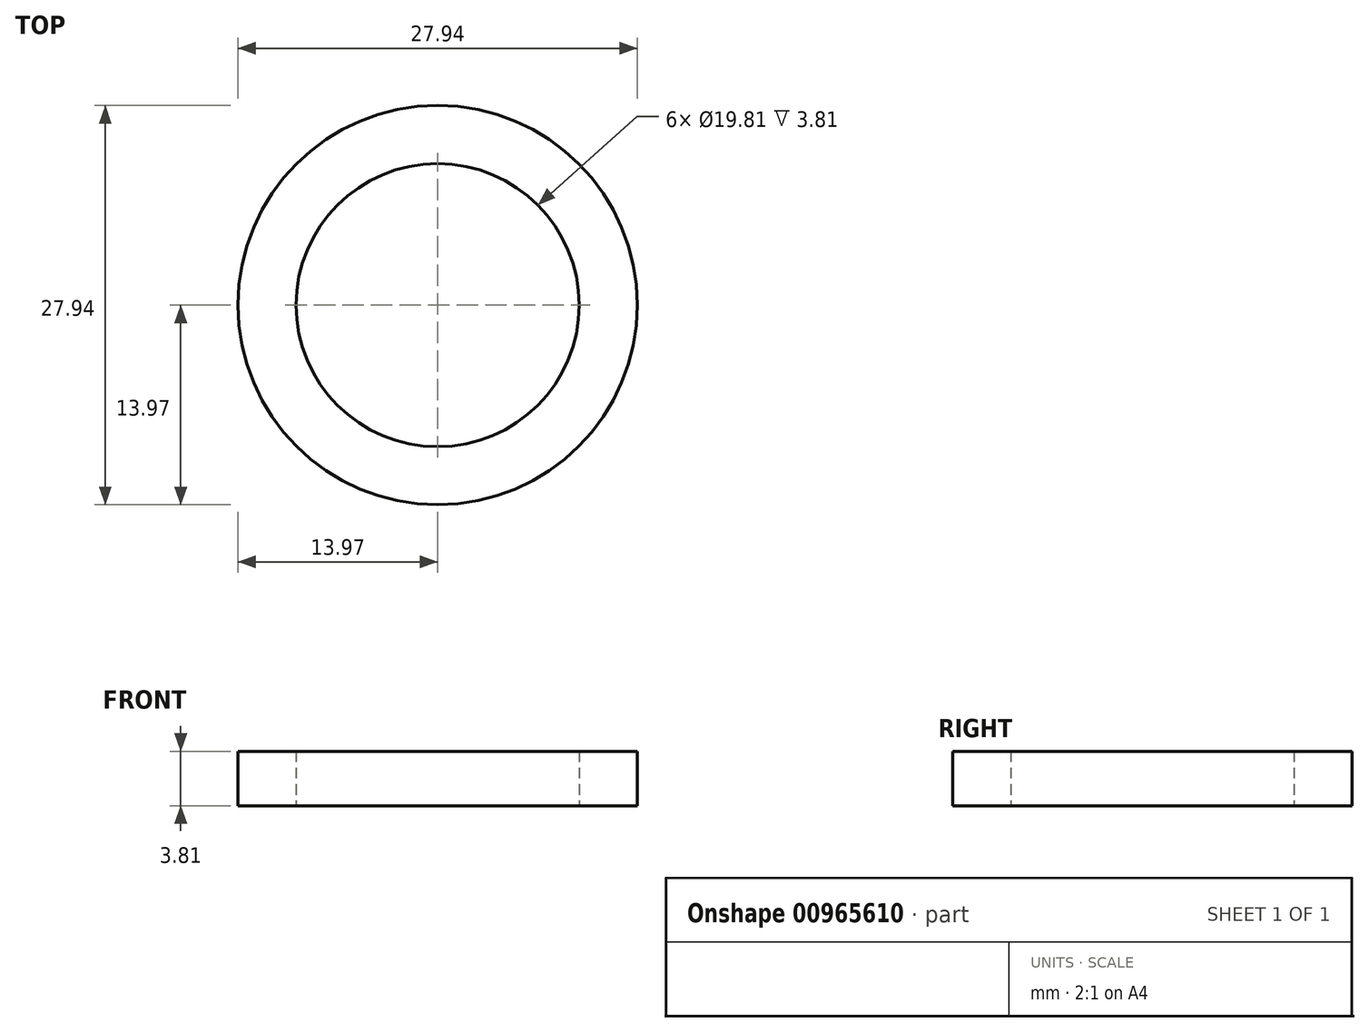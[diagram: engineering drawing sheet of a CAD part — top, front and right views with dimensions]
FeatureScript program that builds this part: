
annotation { "Feature Type Name" : "Feature", "Feature Type Description" : "" }
export const myFeature = defineFeature(function(context is Context, id is Id, definition is map)
    precondition{}
    {
        {
            var Q0;
            Q0=qCreatedBy(makeId("Top.planeOp"),FACE);
            var sketch = newSketch(context, id + "F0", { "sketchPlane" : qUnion([Q0])});
            skCircle(sketch, "E0", {"center": v(0, 0) * mm, "radius": 9.9 * mm});
            skCircle(sketch, "E1", {"center": v(0, 0) * mm, "radius": 13.97 * mm});
            skSolve(sketch);
        }
        {
            var Q0;
            Q0=makeQuery(id+"F0.imprint","IMPRINT",FACE,{"disambiguationData":[TD([[makeQuery(id+"F0.imprint","IMPRINT",EDGE,{"derivedFrom":sQuery(id+"F0.wireOp",EDGE,"E0")}),-1.0]])]});
            extrude(context, id + "F1", {"entities" : qUnion([Q0]), "depth" : 3.8 * mm, "offsetDistance" : 25.4 * mm});
        }
    });
